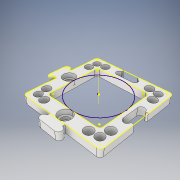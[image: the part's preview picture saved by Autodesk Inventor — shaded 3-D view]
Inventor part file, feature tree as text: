
AUTODESK INVENTOR PART (.ipt)
format: ipt  version: 2019 (Build 230136000, 136)  size: 448,000 bytes
history: native  units: mm
features: sketch x6, projected_geometry x5, extrude x4, mirror x2, pattern_circular x2, other x1, hole x1
ambient origin geometry x8: Origin, YZ Plane, XZ Plane, XY Plane, X Axis, Y Axis, Z Axis, Center Point
bodies: Volumenkörper1 (feature_tree)
feature tree (21):
  extrude  "Extrusion1"  TaperAngle=0.0deg  [1 undecoded]
  mirror  "Mirror6"
  mirror  "Mirror7"
  extrude  "Extrusion13"  TaperAngle=0.0deg  [1 undecoded]
  sketch  "Sketch27"  dims[d9=0.0mm d13=0.0mm]
  extrude  "Extrusion14"  TaperAngle=0.0deg  [1 undecoded]
  other  "Work Axis4"
  pattern_circular  "Circular Pattern6"  [2 undecoded]
  hole  "Hole7"  [1 undecoded]
  extrude  "Extrusion15"  TaperAngle=0.0deg  [1 undecoded]
  pattern_circular  "Circular Pattern7"  [2 undecoded]
  sketch  "Skizze1"  dims[d5=0.0mm d6=0.0mm]
  sketch  "Sketch26"  dims[d7=0.0mm d8=0.0mm]
  projected_geometry  "Projected Loop21"
  projected_geometry  "Projected Loop22"
  sketch  "Sketch28"  dims[d14=0.0mm]
  projected_geometry  "Projected Loop23"
  sketch  "Sketch29"  dims[d20=0.0mm]
  projected_geometry  "Projected Loop24"
  sketch  "Sketch30"  dims[d21=0.0mm d22=0.0mm d23=0.0mm d24=0.0mm d25=3.0mm d26=0.0mm d27=0.0mm d28=0.0mm d29=0.0mm d30=0.0mm d31=0.0mm d32=0.0mm d33=0.0mm d34=0.0mm d46=0.0mm d47=0.0mm d48=0.0mm d49=-10.0mm d50=0.0mm d51=0.0mm d52=0.0mm d53=0.0mm d54=0.0mm d55=0.0mm d56=0.0mm d57=0.0mm d58=0.0mm d59=0.0mm d77=2.65mm d82=2.65mm d222=0.5mm d236=5.3mm d278=25.0mm d279=25.0mm d2=8.0mm d281=8.0mm d282=2.0mm d283=4.85mm d284=20.0mm d4=20.0mm d286=5.3mm d290=20.8mm d292=2.0mm d293=5.5mm d294=14.0mm d295=18.0mm d296=10.0mm d297=1.5mm d298=10.0mm d299=0.0mm d300=2.0mm d301=0.5mm d302=10.0mm d303=0.0mm d307=0.075mm d308=20.0mm d309=90.0deg d313=6.3mm d314=6.3mm d315=0.194632mm d316=0.0mm d317=0.0mm d318=0.090102mm d319=7.78mm d320=4.0mm d321=21.4mm d322=4.0mm d323=5.0mm d324=6.0mm d325=8.0mm d326=3.0mm d327=90.0deg d328=8.0mm d329=20.594885mm d330=0.0mm d331=0.0mm d332=0.0mm d334=14.0mm d336=10.0mm d337=1.5mm d338=2.0mm d339=0.5mm d340=0.075mm d341=0.075mm d342=0.075mm d343=0.075mm d344=10.0mm d345=0.0mm d346=0.075mm d347=0.0mm d348=20.0mm d349=90.0deg]
  projected_geometry  "Projected Loop25"
note: 9 required parameter values undecoded (feature->parameter linkage not recoverable at this tier; creation-order binding heuristic only, values carry confidence <= 0.55)
